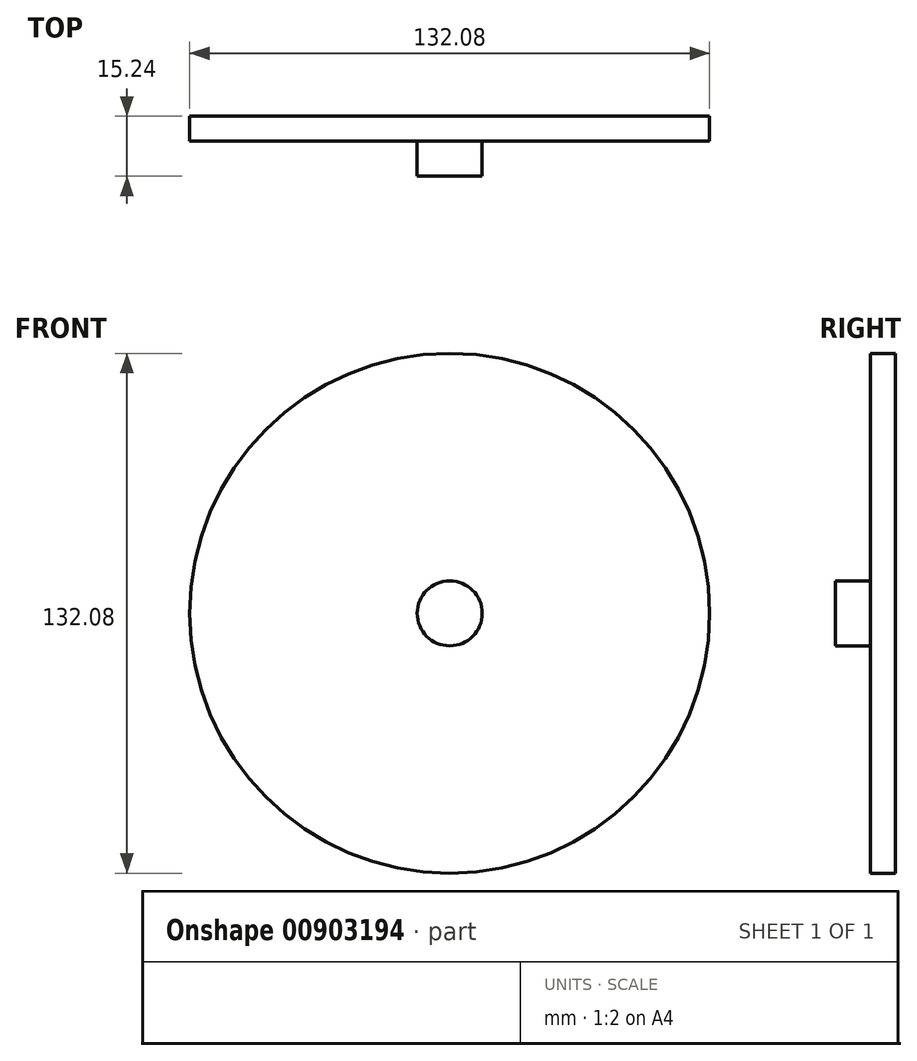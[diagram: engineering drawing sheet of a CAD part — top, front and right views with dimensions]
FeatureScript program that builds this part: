
annotation { "Feature Type Name" : "Feature", "Feature Type Description" : "" }
export const myFeature = defineFeature(function(context is Context, id is Id, definition is map)
    precondition{}
    {
        {
            var Q0;
            Q0=qCreatedBy(makeId("Front.planeOp"),FACE);
            var sketch = newSketch(context, id + "F0", { "sketchPlane" : qUnion([Q0])});
            skCircle(sketch, "E0", {"center": v(0, 0) * mm, "radius": 66.04 * mm});
            skSolve(sketch);
        }
        {
            var Q0;
            Q0=makeQuery(id+"F0.imprint","IMPRINT",FACE,{"disambiguationData":[TD([[makeQuery(id+"F0.imprint","IMPRINT",EDGE,{"derivedFrom":sQuery(id+"F0.wireOp",EDGE,"E0")}),1.0]])]});
            var Q1;
            Q1=makeQuery(id+"F0.imprint","IMPRINT",FACE,{"disambiguationData":[TD([[makeQuery(id+"F0.imprint","IMPRINT",EDGE,{"derivedFrom":sQuery(id+"F0.wireOp",EDGE,"vNChoAXl-o70u-5Zlr-F31U-SLRtnB67If6W")}),1.0]])]});
            extrude(context, id + "F1", {"entities" : qUnion([Q0, Q1]), "depth" : 6.35 * mm, "offsetDistance" : 25.4 * mm});
        }
        {
            var Q0;
            Q0=qCreatedBy(makeId("Front.planeOp"),FACE);
            var sketch = newSketch(context, id + "F2", { "sketchPlane" : qUnion([Q0])});
            skCircle(sketch, "E1", {"center": v(0, 0) * mm, "radius": 8.26 * mm});
            skSolve(sketch);
        }
        {
            var Q0;
            Q0 = qSketchRegion(id + "F2", true);
            extrude(context, id + "F3", {"entities" : qUnion([Q0]), "operationType" : NewBodyOperationType.ADD, "depth" : 15.24 * mm, "offsetDistance" : 25.4 * mm});
        }
    });
